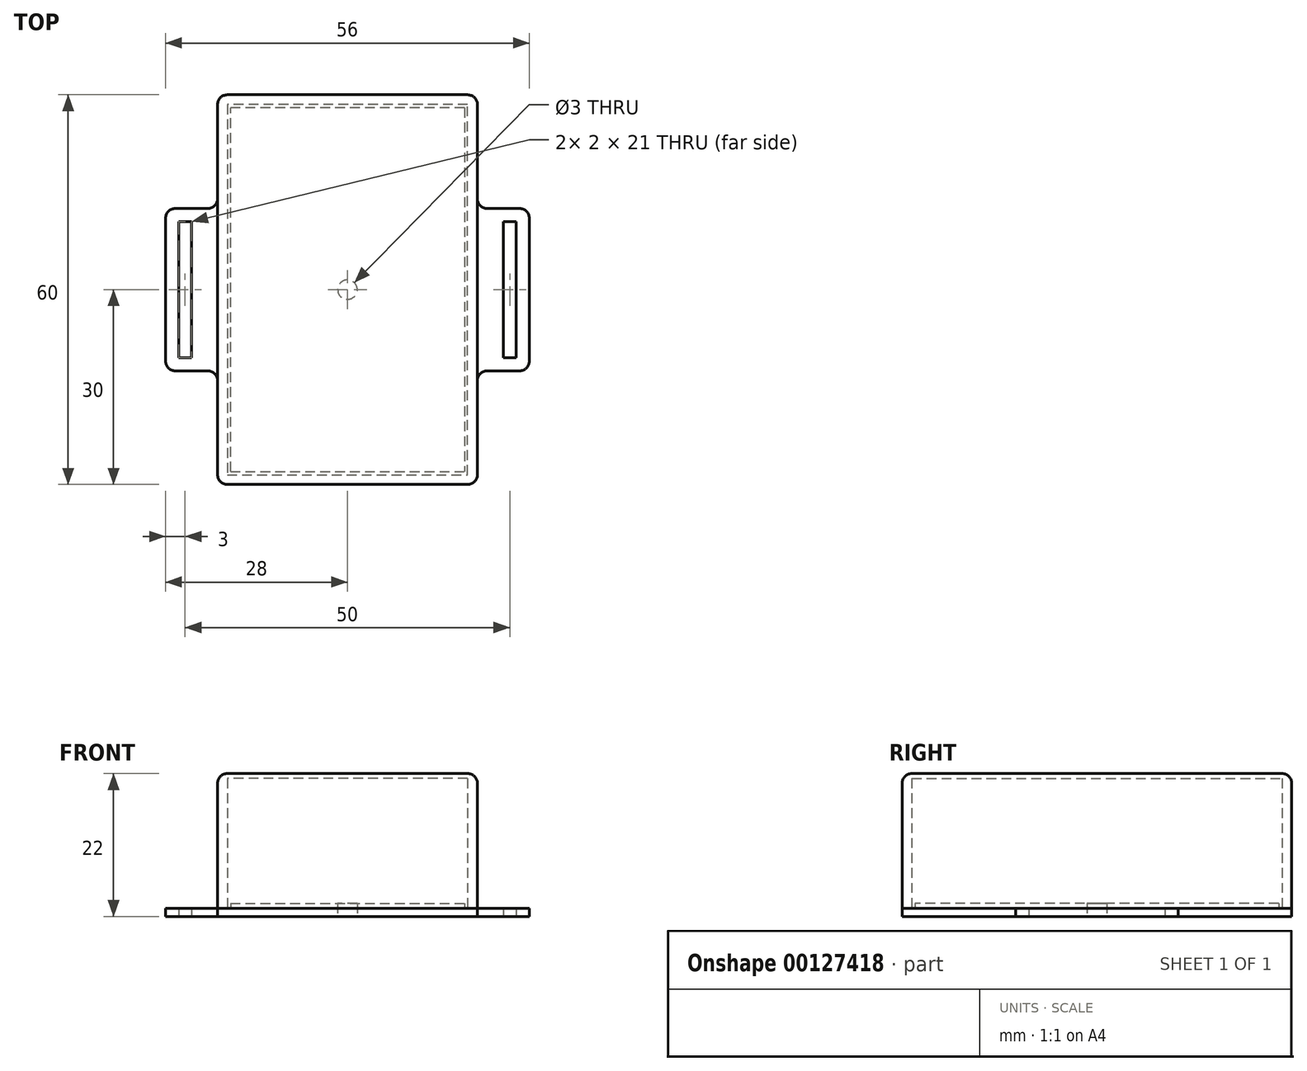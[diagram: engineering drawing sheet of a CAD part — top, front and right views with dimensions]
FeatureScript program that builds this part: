
annotation { "Feature Type Name" : "Feature", "Feature Type Description" : "" }
export const myFeature = defineFeature(function(context is Context, id is Id, definition is map)
    precondition{}
    {
        {
            assignVariable(context, id + "F0", {"name" : "h", "anyValue" : 20});
        }
        {
            assignVariable(context, id + "F1", {"name" : "layer", "anyValue" : .25});
        }
        {
            assignVariable(context, id + "F2", {"name" : "nozw", "anyValue" : .5});
        }
        {
            var Q0;
            Q0=qCreatedBy(makeId("Top.planeOp"),FACE);
            var sketch = newSketch(context, id + "F3", { "sketchPlane" : qUnion([Q0])});
            skLineSegment(sketch, "E0", {"start": v(0, 30) * mm, "end": v(20, 30) * mm});
            skLineSegment(sketch, "E1", {"start": v(20, 30) * mm, "end": v(20, 0) * mm});
            skLineSegment(sketch, "E2", {"start": v(20, 12.5) * mm, "end": v(28, 12.5) * mm});
            skLineSegment(sketch, "E3", {"start": v(28, 12.5) * mm, "end": v(28, 0) * mm});
            skLineSegment(sketch, "E4", {"start": v(24, 0) * mm, "end": v(24, 10.5) * mm});
            skLineSegment(sketch, "E5", {"start": v(24, 10.5) * mm, "end": v(26, 10.5) * mm});
            skLineSegment(sketch, "E6", {"start": v(26, 10.5) * mm, "end": v(26, 0) * mm});
            skLineSegment(sketch, "E7.MirrorCS", {"start": v(26, -10.5) * mm, "end": v(26, 0) * mm});
            skLineSegment(sketch, "E8.MirrorCS", {"start": v(24, -10.5) * mm, "end": v(26, -10.5) * mm});
            skLineSegment(sketch, "E9.MirrorCS", {"start": v(24, 0) * mm, "end": v(24, -10.5) * mm});
            skLineSegment(sketch, "E10.MirrorCS", {"start": v(0, -30) * mm, "end": v(20, -30) * mm});
            skLineSegment(sketch, "E11.MirrorCS", {"start": v(28, -12.5) * mm, "end": v(28, 0) * mm});
            skLineSegment(sketch, "E12.MirrorCS", {"start": v(20, -30) * mm, "end": v(20, 0) * mm});
            skLineSegment(sketch, "E13.MirrorCS", {"start": v(20, -12.5) * mm, "end": v(28, -12.5) * mm});
            skLineSegment(sketch, "E14.MirrorCS", {"start": v(-24, 0) * mm, "end": v(-24, 10.5) * mm});
            skLineSegment(sketch, "E15.MirrorCS", {"start": v(-24, 10.5) * mm, "end": v(-26, 10.5) * mm});
            skLineSegment(sketch, "E16.MirrorCS", {"start": v(-26, 10.5) * mm, "end": v(-26, 0) * mm});
            skLineSegment(sketch, "E17.MirrorCS", {"start": v(-26, -10.5) * mm, "end": v(-26, 0) * mm});
            skLineSegment(sketch, "E18.MirrorCS", {"start": v(-24, -10.5) * mm, "end": v(-26, -10.5) * mm});
            skLineSegment(sketch, "E19.MirrorCS", {"start": v(-24, 0) * mm, "end": v(-24, -10.5) * mm});
            skLineSegment(sketch, "E20.MirrorCS", {"start": v(0, -30) * mm, "end": v(-20, -30) * mm});
            skLineSegment(sketch, "E21.MirrorCS", {"start": v(-20, -30) * mm, "end": v(-20, 0) * mm});
            skLineSegment(sketch, "E22.MirrorCS", {"start": v(-28, 12.5) * mm, "end": v(-28, 0) * mm});
            skLineSegment(sketch, "E23.MirrorCS", {"start": v(-20, 12.5) * mm, "end": v(-28, 12.5) * mm});
            skLineSegment(sketch, "E24.MirrorCS", {"start": v(-20, 30) * mm, "end": v(-20, 0) * mm});
            skLineSegment(sketch, "E25.MirrorCS", {"start": v(-28, -12.5) * mm, "end": v(-28, 0) * mm});
            skLineSegment(sketch, "E26.MirrorCS", {"start": v(-20, -12.5) * mm, "end": v(-28, -12.5) * mm});
            skLineSegment(sketch, "E27.MirrorCS", {"start": v(0, 30) * mm, "end": v(-20, 30) * mm});
            skLineSegment(sketch, "E28.0", {"start": v(0, 28) * mm, "end": v(18, 28) * mm});
            skLineSegment(sketch, "E28.1", {"start": v(18, 28) * mm, "end": v(18, 0) * mm});
            skLineSegment(sketch, "E28.2", {"start": v(0, 28) * mm, "end": v(-18, 28) * mm});
            skLineSegment(sketch, "E28.3", {"start": v(18, -28) * mm, "end": v(18, 0) * mm});
            skLineSegment(sketch, "E28.4", {"start": v(-18, 28) * mm, "end": v(-18, 0) * mm});
            skLineSegment(sketch, "E28.5", {"start": v(-18, -28) * mm, "end": v(-18, 0) * mm});
            skLineSegment(sketch, "E28.6", {"start": v(0, -28) * mm, "end": v(-18, -28) * mm});
            skLineSegment(sketch, "E28.7", {"start": v(0, -28) * mm, "end": v(18, -28) * mm});
            skCircle(sketch, "E29", {"center": v(0, 0) * mm, "radius": 1.5 * mm});
            skSolve(sketch);
        }
        {
            var Q0;
            Q0=makeQuery(id+"F3.imprint","IMPRINT",FACE,{"disambiguationData":[TD([[makeQuery(id+"F3.imprint","IMPRINT",EDGE,{"derivedFrom":sQuery(id+"F3.wireOp",EDGE,"E14.MirrorCS")}),-1.0]])]});
            var Q1;
            {var subQ4=sQuery(id+"F3.wireOp",EDGE,"E2");Q1=makeQuery(id+"F3.imprint","IMPRINT",FACE,{"disambiguationData":[TD([[makeQuery(id+"F3.imprint","IMPRINT",EDGE,{"derivedFrom":subQ4}),-1.0]])]});}
            var Q2;
            {var subQ11=sQuery(id+"F3.wireOp",EDGE,"E0");Q2=makeQuery(id+"F3.imprint","IMPRINT",FACE,{"disambiguationData":[TD([[makeQuery(id+"F3.imprint","IMPRINT",EDGE,{"derivedFrom":subQ11}),-1.0]])]});}
            extrude(context, id + "F4", {"entities" : qUnion([Q0, Q1, Q2]), "depth" : (getVariable(context, 'layer') * 5) * mm});
        }
        {
            var Q0;
            Q0=makeQuery(id+"F3.imprint","IMPRINT",FACE,{"disambiguationData":[TD([[makeQuery(id+"F3.imprint","IMPRINT",EDGE,{"derivedFrom":sQuery(id+"F3.wireOp",EDGE,"E28.0")}),-1.0]])]});
            extrude(context, id + "F5", {"entities" : qUnion([Q0]), "operationType" : NewBodyOperationType.ADD, "depth" : (getVariable(context, 'layer') * 8) * mm});
        }
        {
            var Q0;
            Q0=qCreatedBy(makeId("Top.planeOp"),FACE);
            cPlane(context, id + "F6", {"entities" : qUnion([Q0]), "cplaneType" : CPlaneType.OFFSET, "offset" : (getVariable(context, 'layer') * 5) * mm, "width" : 150 * mm, "height" : 150 * mm});
        }
        {
            var Q0;
            Q0=qCreatedBy(id+"F6.planeOp",FACE);
            var sketch = newSketch(context, id + "F7", { "sketchPlane" : qUnion([Q0])});
            skLineSegment(sketch, "E30.0.0", {"start": v(20, 30) * mm, "end": v(-20, 30) * mm});
            skLineSegment(sketch, "E30.0.1", {"start": v(-20, 30) * mm, "end": v(-20, -30) * mm});
            skLineSegment(sketch, "E30.0.2", {"start": v(-20, -30) * mm, "end": v(20, -30) * mm});
            skLineSegment(sketch, "E30.0.3", {"start": v(20, -30) * mm, "end": v(20, 30) * mm});
            skLineSegment(sketch, "E31.0", {"start": v(18.5, 28.5) * mm, "end": v(-18.5, 28.5) * mm});
            skLineSegment(sketch, "E31.1", {"start": v(18.5, -28.5) * mm, "end": v(18.5, 28.5) * mm});
            skLineSegment(sketch, "E31.2", {"start": v(-18.5, -28.5) * mm, "end": v(18.5, -28.5) * mm});
            skLineSegment(sketch, "E31.3", {"start": v(-18.5, 28.5) * mm, "end": v(-18.5, -28.5) * mm});
            skSolve(sketch);
        }
        {
            var Q0;
            Q0=makeQuery(id+"F7.imprint","IMPRINT",FACE,{"disambiguationData":[TD([[makeQuery(id+"F7.imprint","IMPRINT",EDGE,{"derivedFrom":sQuery(id+"F7.wireOp",EDGE,"E30.0.0")}),1.0]])]});
            extrude(context, id + "F8", {"entities" : qUnion([Q0]), "depth" : (getVariable(context, 'h')) * mm});
        }
        {
            var Q0;
            Q0=makeQuery(id+"F8.opExtrude","CAP_FACE",FACE,{"disambiguationData":[OSD([sQuery(id+"F7.wireOp",EDGE,"E30.0.0"),sQuery(id+"F7.wireOp",EDGE,"E30.0.1"),sQuery(id+"F7.wireOp",EDGE,"E30.0.2"),sQuery(id+"F7.wireOp",EDGE,"E30.0.3"),sQuery(id+"F7.wireOp",EDGE,"E31.0"),sQuery(id+"F7.wireOp",EDGE,"E31.1"),sQuery(id+"F7.wireOp",EDGE,"E31.2"),sQuery(id+"F7.wireOp",EDGE,"E31.3")])],"isStart":false});
            var sketch = newSketch(context, id + "F9", { "sketchPlane" : qUnion([Q0])});
            skLineSegment(sketch, "E32.0.0", {"start": v(20, -30) * mm, "end": v(20, 30) * mm});
            skLineSegment(sketch, "E32.0.1", {"start": v(20, 30) * mm, "end": v(-20, 30) * mm});
            skLineSegment(sketch, "E32.0.2", {"start": v(-20, 30) * mm, "end": v(-20, -30) * mm});
            skLineSegment(sketch, "E32.0.3", {"start": v(-20, -30) * mm, "end": v(20, -30) * mm});
            skSolve(sketch);
        }
        {
            var Q0;
            Q0=makeQuery(id+"F9.imprint","IMPRINT",FACE,{"disambiguationData":[TD([[makeQuery(id+"F9.imprint","IMPRINT",EDGE,{"derivedFrom":sQuery(id+"F9.wireOp",EDGE,"E32.0.0")}),1.0]])]});
            var Q1;
            Q1=makeQuery(id+"F9.imprint","IMPRINT",FACE,{"disambiguationData":[TD([[makeQuery(id+"F9.imprint","IMPRINT",EDGE,{"derivedFrom":makeQuery(id+"F8.opExtrude","CAP_EDGE",EDGE,{"disambiguationData":[OSD([sQuery(id+"F7.wireOp",EDGE,"E31.0")])],"isStart":false})}),1.0]])]});
            extrude(context, id + "F10", {"entities" : qUnion([Q0, Q1]), "operationType" : NewBodyOperationType.ADD, "depth" : (getVariable(context, 'layer') * 3) * mm});
        }
        {
            var Q0;
            Q0=makeQuery(id+"F10.opExtrude","CAP_EDGE",EDGE,{"disambiguationData":[OSD([sQuery(id+"F9.wireOp",EDGE,"E32.0.3")])],"isStart":false});
            var Q1;
            Q1=makeQuery(id+"F10.opExtrude","CAP_EDGE",EDGE,{"disambiguationData":[OSD([sQuery(id+"F9.wireOp",EDGE,"E32.0.2")])],"isStart":false});
            var Q2;
            Q2=makeQuery(id+"F10.opExtrude","CAP_EDGE",EDGE,{"disambiguationData":[OSD([sQuery(id+"F9.wireOp",EDGE,"E32.0.1")])],"isStart":false});
            var Q3;
            Q3=makeQuery(id+"F10.opExtrude","CAP_EDGE",EDGE,{"disambiguationData":[OSD([sQuery(id+"F9.wireOp",EDGE,"E32.0.0")])],"isStart":false});
            var Q4;
            Q4=makeQuery(id+"F10.boolean.opBoolean","MERGE",EDGE,{"derivedFrom":[makeQuery(id+"F8.opExtrude","SWEPT_EDGE",EDGE,{"disambiguationData":[OSD([sQuery(id+"F7.wireOp",EDGE,"E30.0.2"),sQuery(id+"F7.wireOp",EDGE,"E30.0.3")])]}),makeQuery(id+"F10.opExtrude","SWEPT_EDGE",EDGE,{"disambiguationData":[OSD([sQuery(id+"F9.wireOp",EDGE,"E32.0.0"),sQuery(id+"F9.wireOp",EDGE,"E32.0.3")])]})]});
            var Q5;
            Q5=makeQuery(id+"F10.boolean.opBoolean","MERGE",EDGE,{"derivedFrom":[makeQuery(id+"F8.opExtrude","SWEPT_EDGE",EDGE,{"disambiguationData":[OSD([sQuery(id+"F7.wireOp",EDGE,"E30.0.0"),sQuery(id+"F7.wireOp",EDGE,"E30.0.3")])]}),makeQuery(id+"F10.opExtrude","SWEPT_EDGE",EDGE,{"disambiguationData":[OSD([sQuery(id+"F9.wireOp",EDGE,"E32.0.0"),sQuery(id+"F9.wireOp",EDGE,"E32.0.1")])]})]});
            var Q6;
            Q6=makeQuery(id+"F10.boolean.opBoolean","MERGE",EDGE,{"derivedFrom":[makeQuery(id+"F8.opExtrude","SWEPT_EDGE",EDGE,{"disambiguationData":[OSD([sQuery(id+"F7.wireOp",EDGE,"E30.0.1"),sQuery(id+"F7.wireOp",EDGE,"E30.0.2")])]}),makeQuery(id+"F10.opExtrude","SWEPT_EDGE",EDGE,{"disambiguationData":[OSD([sQuery(id+"F9.wireOp",EDGE,"E32.0.2"),sQuery(id+"F9.wireOp",EDGE,"E32.0.3")])]})]});
            var Q7;
            Q7=makeQuery(id+"F10.boolean.opBoolean","MERGE",EDGE,{"derivedFrom":[makeQuery(id+"F8.opExtrude","SWEPT_EDGE",EDGE,{"disambiguationData":[OSD([sQuery(id+"F7.wireOp",EDGE,"E30.0.0"),sQuery(id+"F7.wireOp",EDGE,"E30.0.1")])]}),makeQuery(id+"F10.opExtrude","SWEPT_EDGE",EDGE,{"disambiguationData":[OSD([sQuery(id+"F9.wireOp",EDGE,"E32.0.1"),sQuery(id+"F9.wireOp",EDGE,"E32.0.2")])]})]});
            var Q8;
            Q8=makeQuery(id+"F4.opExtrude","SWEPT_EDGE",EDGE,{"disambiguationData":[OSD([sQuery(id+"F3.wireOp",EDGE,"E24.MirrorCS"),sQuery(id+"F3.wireOp",EDGE,"E27.MirrorCS")])]});
            var Q9;
            Q9=makeQuery(id+"F4.opExtrude","SWEPT_EDGE",EDGE,{"disambiguationData":[OSD([sQuery(id+"F3.wireOp",EDGE,"E0"),sQuery(id+"F3.wireOp",EDGE,"E1")])]});
            var Q10;
            Q10=makeQuery(id+"F4.opExtrude","SWEPT_EDGE",EDGE,{"disambiguationData":[OSD([sQuery(id+"F3.wireOp",EDGE,"E20.MirrorCS"),sQuery(id+"F3.wireOp",EDGE,"E21.MirrorCS")])]});
            var Q11;
            Q11=makeQuery(id+"F4.opExtrude","SWEPT_EDGE",EDGE,{"disambiguationData":[OSD([sQuery(id+"F3.wireOp",EDGE,"E25.MirrorCS"),sQuery(id+"F3.wireOp",EDGE,"E26.MirrorCS")])]});
            var Q12;
            Q12=makeQuery(id+"F4.opExtrude","SWEPT_EDGE",EDGE,{"disambiguationData":[OSD([sQuery(id+"F3.wireOp",EDGE,"E22.MirrorCS"),sQuery(id+"F3.wireOp",EDGE,"E23.MirrorCS")])]});
            var Q13;
            Q13=makeQuery(id+"F4.opExtrude","SWEPT_EDGE",EDGE,{"disambiguationData":[OSD([sQuery(id+"F3.wireOp",EDGE,"E23.MirrorCS"),sQuery(id+"F3.wireOp",EDGE,"E24.MirrorCS")])]});
            var Q14;
            Q14=makeQuery(id+"F4.opExtrude","SWEPT_EDGE",EDGE,{"disambiguationData":[OSD([sQuery(id+"F3.wireOp",EDGE,"E21.MirrorCS"),sQuery(id+"F3.wireOp",EDGE,"E26.MirrorCS")])]});
            var Q15;
            Q15=makeQuery(id+"F4.opExtrude","SWEPT_EDGE",EDGE,{"disambiguationData":[OSD([sQuery(id+"F3.wireOp",EDGE,"E10.MirrorCS"),sQuery(id+"F3.wireOp",EDGE,"E12.MirrorCS")])]});
            var Q16;
            Q16=makeQuery(id+"F4.opExtrude","SWEPT_EDGE",EDGE,{"disambiguationData":[OSD([sQuery(id+"F3.wireOp",EDGE,"E11.MirrorCS"),sQuery(id+"F3.wireOp",EDGE,"E13.MirrorCS")])]});
            var Q17;
            Q17=makeQuery(id+"F4.opExtrude","SWEPT_EDGE",EDGE,{"disambiguationData":[OSD([sQuery(id+"F3.wireOp",EDGE,"E12.MirrorCS"),sQuery(id+"F3.wireOp",EDGE,"E13.MirrorCS")])]});
            var Q18;
            Q18=makeQuery(id+"F4.opExtrude","SWEPT_EDGE",EDGE,{"disambiguationData":[OSD([sQuery(id+"F3.wireOp",EDGE,"E2"),sQuery(id+"F3.wireOp",EDGE,"E3")])]});
            var Q19;
            Q19=makeQuery(id+"F4.opExtrude","SWEPT_EDGE",EDGE,{"disambiguationData":[OSD([sQuery(id+"F3.wireOp",EDGE,"E1"),sQuery(id+"F3.wireOp",EDGE,"E2")])]});
            fillet(context, id + "F11", {"entities" : qUnion([Q0, Q1, Q2, Q3, Q4, Q5, Q6, Q7, Q8, Q9, Q10, Q11, Q12, Q13, Q14, Q15, Q16, Q17, Q18, Q19]), "radius" : (getVariable(context, 'nozw') * 3) * mm, "tangentPropagation" : true, "allowEdgeOverflow" : false});
        }
    });
